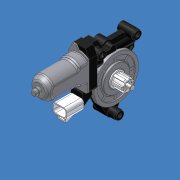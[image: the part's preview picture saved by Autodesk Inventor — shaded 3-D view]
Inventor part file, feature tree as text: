
AUTODESK INVENTOR PART (.ipt)
format: ipt  version: 2014 SP1 (Build 180222100, 222)  size: 1,707,008 bytes
history: native  units: mm (DEFAULTED — no unit token found)
features: sketch x59, extrude x51, fillet x11, chamfer x9, hole x6, pattern_circular x4, revolve x2, plane x2, other x1, mirror x1, projected_geometry x1
ambient origin geometry x8: Origin, YZ Plane, XZ Plane, XY Plane, X Axis, Y Axis, Z Axis, Center Point
bodies: Solid1 (feature_tree)
feature tree (147):
  extrude  "Extrusion1"  Depth=5.0mm TaperAngle=0.0deg
  extrude  "Extrusion2"  Depth=42.0mm
  extrude  "Extrusion3"  Depth=2.0mm
  extrude  "Extrusion4"  Depth=1.0mm
  extrude  "Extrusion5"  Depth=4.0mm
  pattern_circular  "Circular Pattern1"  Count=8 Angle=360.0deg
  extrude  "Extrusion6"  Depth=1.7mm TaperAngle=0.0deg
  extrude  "Extrusion7"  Depth=17.9mm TaperAngle=0.0deg
  hole  "Hole1"  [1 undecoded]
  extrude  "Extrusion8"  Depth=18.0mm TaperAngle=0.0deg
  chamfer  "Chamfer1"  Distance=2.0mm
  pattern_circular  "Circular Pattern2"  Count=6 Angle=360.0deg
  extrude  "Extrusion9"  Depth=12.5mm TaperAngle=0.0deg
  extrude  "Extrusion10"  Depth=2.0mm TaperAngle=0.0deg
  chamfer  "Chamfer2"  Distance=2.0mm
  fillet  "Fillet1"  Radius=0.5mm
  fillet  "Fillet2"  Radius=1.5mm
  extrude  "Extrusion11"  Depth=0.5mm TaperAngle=0.0deg
  extrude  "Extrusion12"  Depth=3.0mm
  extrude  "Extrusion13"  Depth=2.0mm
  revolve  "Revolution1"  [1 undecoded]
  extrude  "Extrusion14"  TaperAngle=30.0deg  [1 undecoded]
  pattern_circular  "Circular Pattern3"  Count=12 Angle=360.0deg
  extrude  "Extrusion15"  Depth=0.5mm
  fillet  "Fillet3"  Radius=43.0mm
  extrude  "Extrusion16"  Depth=2.0mm TaperAngle=0.0deg
  fillet  "Fillet4"  Radius=1.0mm
  hole  "Hole2"  [1 undecoded]
  extrude  "Extrusion18"  Depth=0.9mm
  fillet  "Fillet5"  Radius=120.0mm
  pattern_circular  "Circular Pattern4"  Count=2  [1 undecoded]
  plane  "Work Plane1"
  plane  "Work Plane2"
  other  "Work Axis1"
  extrude  "Extrusion19"  Depth=23.0mm
  extrude  "Extrusion20"  Depth=5.0mm TaperAngle=0.0deg
  extrude  "Extrusion21"  Depth=31.0mm
  extrude  "Extrusion22"  Depth=4.0mm
  extrude  "Extrusion23"  Depth=6.0mm
  fillet  "Fillet6"  Radius=0.2mm
  chamfer  "Chamfer3"  Distance=2.0mm
  chamfer  "Chamfer4"  Distance=15.0mm
  extrude  "Extrusion24"  Depth=17.5mm
  fillet  "Fillet7"  Radius=40.0mm
  extrude  "Extrusion25"  Depth=1.0mm
  extrude  "Extrusion26"  TaperAngle=90.0deg  [1 undecoded]
  chamfer  "Chamfer5"  Distance=43.0mm
  chamfer  "Chamfer6"  Distance=4.0mm
  fillet  "Fillet8"  Radius=9.0mm
  revolve  "Revolution2"  [1 undecoded]
  extrude  "Extrusion27"  Depth=2.0mm TaperAngle=0.0deg
  mirror  "Mirror1"
  fillet  "Fillet9"  Radius=13.2mm
  extrude  "Extrusion28"  Depth=18.0mm TaperAngle=0.0deg
  extrude  "Extrusion29"  Depth=7.0mm
  fillet  "Fillet10"  Radius=50.0mm
  extrude  "Extrusion30"  Depth=14.0mm
  extrude  "Extrusion31"  Depth=8.2mm TaperAngle=0.0deg
  chamfer  "Chamfer8"  Distance=3.0mm
  extrude  "Extrusion32"  Depth=2.0mm
  extrude  "Extrusion33"  Depth=2.0mm TaperAngle=0.0deg
  extrude  "Extrusion34"  Depth=7.0mm
  hole  "Hole3"  [1 undecoded]
  extrude  "Extrusion35"  Depth=2.0mm TaperAngle=0.0deg
  extrude  "Extrusion36"  Depth=15.5mm
  extrude  "Extrusion39"  Depth=5.0mm
  extrude  "Extrusion40"  Depth=2.0mm
  extrude  "Extrusion41"  Depth=16.0mm TaperAngle=0.0deg
  hole  "Hole4"  [1 undecoded]
  extrude  "Extrusion42"  Depth=2.0mm
  extrude  "Extrusion43"  Depth=2.0mm
  extrude  "Extrusion46"  Depth=9.5mm TaperAngle=0.0deg
  extrude  "Extrusion47"  Depth=2.0mm
  extrude  "Extrusion48"  Depth=2.0mm
  hole  "Hole5"  [1 undecoded]
  hole  "Hole6"  [1 undecoded]
  extrude  "Extrusion50"  Depth=3.0mm TaperAngle=0.0deg
  extrude  "Extrusion51"  Depth=2.0mm
  extrude  "Extrusion52"  Depth=2.0mm TaperAngle=0.0deg
  extrude  "Extrusion53"  Depth=2.0mm TaperAngle=0.0deg
  chamfer  "Chamfer9"  Distance=2.0mm
  extrude  "Extrusion55"  Depth=13.0mm TaperAngle=0.0deg
  fillet  "Fillet12"  Radius=18.5mm
  extrude  "Extrusion56"  Depth=9.0mm
  extrude  "Extrusion57"  Depth=2.0mm
  chamfer  "Chamfer10"  Distance=15.0mm
  extrude  "Extrusion59"  Depth=19.0mm
  sketch  "Sketch1"  dims[d0=72.0mm d1=5.0mm d2=0.0mm]
  sketch  "Sketch2"  dims[d3=60.0mm d4=42.0mm]
  sketch  "Sketch3"  dims[d5=2.0mm d6=0.0mm d7=2.0mm]
  sketch  "Sketch4"  dims[d8=1.0mm d9=0.0mm d10=26.0mm]
  sketch  "Sketch5"  dims[d11=0.5mm d12=0.0mm d13=4.0mm]
  sketch  "Sketch6"  dims[d14=8.0mm]
  sketch  "Sketch7"  dims[d15=22.0mm]
  sketch  "Sketch8"  dims[d16=1.5mm d17=0.0mm]
  sketch  "Sketch9"  dims[d18=2.0mm d19=80.0mm d21=360.0deg]
  sketch  "Sketch10"  dims[d22=23.9mm d23=1.7mm d24=0.0mm]
  sketch  "Sketch11"  dims[d25=16.2mm d26=17.9mm d27=0.0mm]
  sketch  "Sketch12"  dims[d28=13.0mm d29=6.0mm d30=4.0mm d31=2.0mm d32=14.3117mm d33=2.0mm d34=0.0mm d35=4.0mm]
  sketch  "Sketch13"  dims[d36=10.0mm d37=18.0mm d38=0.0mm d39=2.0mm d40=2.0mm d41=60.0mm d43=360.0deg]
  sketch  "Sketch14"  dims[d44=12.5mm d45=0.2mm d46=0.0mm]
  sketch  "Sketch15"  dims[d47=8.0mm d48=8.2mm d49=0.0mm d50=0.5mm d51=2.0mm d52=0.5mm d53=1.5mm]
  sketch  "Sketch16"  dims[d54=71.0mm d55=0.5mm d56=0.0mm]
  sketch  "Sketch17"  dims[d57=3.0mm d58=0.0mm d59=68.0mm]
  sketch  "Sketch18"  dims[d60=14.0mm d61=0.0mm d62=2.0mm]
  sketch  "Sketch19"  dims[d63=3.5mm d64=10.0mm]
  sketch  "Sketch21"  dims[d65=90.0deg d66=30.0deg]
  sketch  "Sketch22"  dims[d67=1.0mm]
  sketch  "Sketch23"  dims[d68=1.0mm]
  sketch  "Sketch24"  dims[d69=4.5mm d70=0.0mm d71=120.0mm d73=360.0deg]
  sketch  "Sketch25"  dims[d74=0.5mm d75=0.0mm d76=0.5mm d77=43.0mm]
  sketch  "Sketch26"  dims[d78=2.0mm d79=2.0mm d80=0.0mm d81=1.0mm]
  sketch  "Sketch27"  dims[d82=2.6mm d83=6.0mm d84=4.0mm d85=2.0mm d86=14.3117mm d87=8.0mm d88=0.0mm d93=2.0mm]
  sketch  "Sketch28"  dims[d94=15.5mm d95=0.0mm d96=0.9mm d97=120.0mm d99=360.0deg]
  sketch  "Sketch29"  dims[d100=-12.0mm d101=-33.88mm]
  sketch  "Sketch30"  dims[d102=15.0mm]
  projected_geometry  "Projected Loop1"
  sketch  "Sketch31"  dims[d103=35.0mm d104=0.0mm d105=20.0mm d106=0.0mm]
  sketch  "Sketch32"  dims[d108=14.5mm d109=0.0mm d110=23.0mm]
  sketch  "Sketch33"  dims[d111=12.25mm d112=5.0mm d113=0.0mm]
  sketch  "Sketch35"  dims[d114=60.0mm d115=31.0mm]
  sketch  "Sketch36"  dims[d116=12.5mm d117=0.0mm d118=4.0mm]
  sketch  "Sketch37"  dims[d119=12.0mm d120=6.0mm d121=6.0mm d122=12.0mm d123=0.2mm]
  sketch  "Sketch38"  dims[d124=0.2mm]
  sketch  "Sketch39"  dims[d125=0.2mm]
  sketch  "Sketch40"  dims[d126=120.0deg d127=2.0mm d128=0.0mm]
  sketch  "Sketch41"  dims[d129=1.0mm]
  sketch  "Sketch43"  dims[d130=40.0mm d131=15.0mm d132=0.0mm]
  sketch  "Sketch46"  dims[d133=35.0mm d134=17.5mm d135=40.0mm d136=0.0mm]
  sketch  "Sketch47"  dims[d137=2.5mm d138=12.0mm d139=1.0mm d140=12.0mm]
  sketch  "Sketch48"  dims[d143=4.0mm d144=90.0deg d145=43.0mm d146=0.0mm]
  sketch  "Sketch49"  dims[d147=8.0mm]
  sketch  "Sketch50"  dims[d148=12.0mm]
  sketch  "Sketch51"  dims[d149=4.0mm]
  sketch  "Sketch54"  dims[d150=10.0mm d151=4.0mm d152=0.0mm d153=9.0mm]
  sketch  "Sketch55"  dims[d154=5.0mm d155=0.0mm d156=1.0mm]
  sketch  "Sketch56"  dims[d157=0.5mm d158=2.0mm d159=0.0mm d160=13.2mm]
  sketch  "Sketch57"  dims[d161=30.0mm d162=18.0mm d163=0.0mm]
  sketch  "Sketch58"  dims[d164=9.0mm d165=14.0mm d166=7.0mm d167=50.0mm d168=0.0mm]
  sketch  "Sketch60"  dims[d169=14.88mm d170=14.0mm]
  sketch  "Sketch61"  dims[d171=20.71mm d172=8.2mm d173=0.0mm]
  sketch  "Sketch63"  dims[d174=12.3mm d175=3.0mm d176=0.0mm]
  sketch  "Sketch66"  dims[d177=4.8mm d178=6.0mm d179=6.2mm d180=2.0mm d181=14.3117mm d182=8.0mm d183=0.0mm d184=22.68928mm]
  sketch  "Sketch68"  dims[d185=4.0mm d186=2.0mm d187=0.0mm]
  sketch  "Sketch69"  dims[d191=7.0mm d192=0.0mm d199=56.58mm]
  sketch  "Sketch70"  dims[d200=14.8mm d201=0.0mm d202=12.3mm]
  sketch  "Sketch72"  dims[d203=3.0mm d204=0.0mm d205=8.0mm d206=0.0mm d207=4.8mm d208=6.0mm d209=6.2mm d210=2.0mm d211=14.3117mm d212=8.0mm d213=0.0mm d214=15.5mm d215=5.0mm d216=41.0mm d217=16.0mm d218=0.0mm d219=9.0mm d220=3.5mm d221=6.25mm d222=9.5mm d223=0.0mm d230=14.2mm d231=48.4mm d232=14.8mm d233=0.0mm d234=12.3mm d235=3.0mm d236=0.0mm d237=16.5mm d238=17.5mm d239=0.0mm d240=4.8mm d241=6.0mm d242=6.2mm d243=2.0mm d244=14.3117mm d245=28.0mm d246=20.594885mm d247=4.134mm d248=6.0mm d249=4.9mm d250=2.0mm d251=14.3117mm d252=8.0mm d253=0.0mm d259=2.0mm d260=0.0mm d261=2.0mm d262=0.0mm d263=13.0mm d264=0.0mm d270=18.5mm d271=0.0mm d272=9.0mm d273=13.0mm d280=2.0mm d281=15.0mm d282=19.0mm d284=23.0mm d285=15.5mm d286=7.5mm d287=27.3mm d288=0.0mm d289=5.0mm d290=1.6mm d291=24.3mm d292=0.0mm d293=13.8mm d294=3.0mm d295=7.0mm d296=0.0mm d302=5.0mm d303=10.0mm d304=9.0mm d305=2.0mm d306=12.5mm d307=0.0mm d308=20.0mm d309=2.0mm d310=2.0mm d311=45.0deg d312=45.0deg d313=45.0deg d314=45.0deg d315=45.0deg d316=45.0deg d317=45.0deg d318=45.0deg d319=45.0deg]
note: 11 required parameter values undecoded (feature->parameter linkage not recoverable at this tier; creation-order binding heuristic only, values carry confidence <= 0.55)